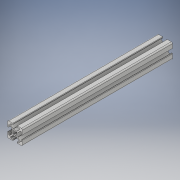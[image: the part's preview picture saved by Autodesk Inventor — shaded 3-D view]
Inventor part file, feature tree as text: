
AUTODESK INVENTOR PART (.ipt)
format: ipt  version: 2019 (Build 230136000, 136)  size: 239,616 bytes
history: native  units: mm
features: extrude x1, sketch x1
ambient origin geometry x8: Origin, YZ Plane, XZ Plane, XY Plane, X Axis, Y Axis, Z Axis, Center Point
bodies: Solid1 (feature_tree)
feature tree (2):
  extrude  "Extrusion1"  [1 undecoded]
  sketch  "Sketch_1"  dims[d0=200.0mm d1=0.0mm]
note: 1 required parameter value undecoded (feature->parameter linkage not recoverable at this tier; creation-order binding heuristic only, values carry confidence <= 0.55)
